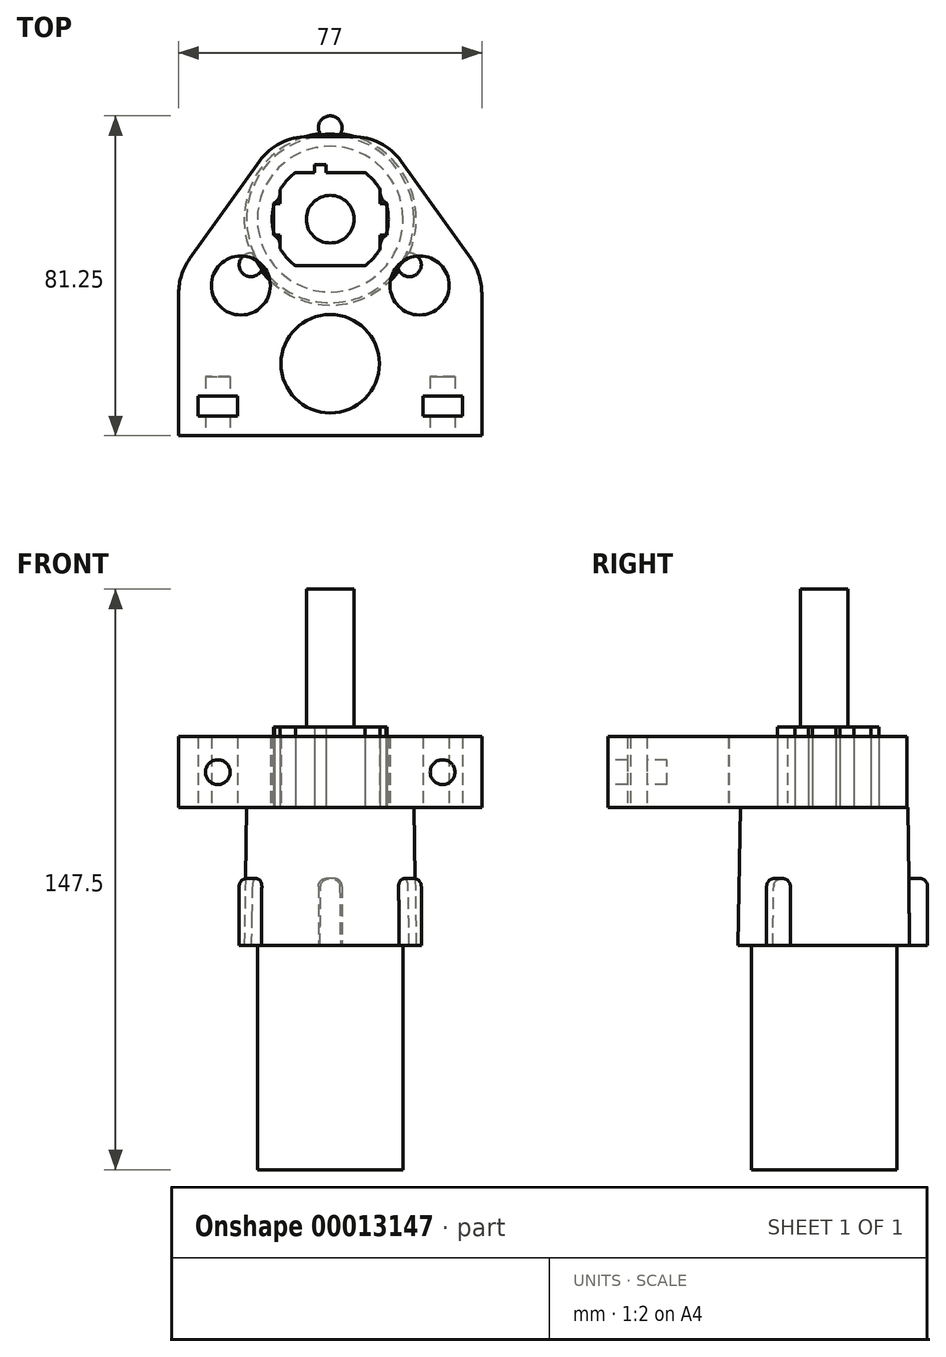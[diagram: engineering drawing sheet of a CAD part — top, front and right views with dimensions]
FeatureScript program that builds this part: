
annotation { "Feature Type Name" : "Feature", "Feature Type Description" : "" }
export const myFeature = defineFeature(function(context is Context, id is Id, definition is map)
    precondition{}
    {
        {
            var Q0;
            Q0=qCreatedBy(makeId("Top.planeOp"),FACE);
            var sketch = newSketch(context, id + "F0", { "sketchPlane" : qUnion([Q0])});
            skCircle(sketch, "E0", {"center": v(0, 0) * mm, "radius": 18.5 * mm});
            skSolve(sketch);
        }
        {
            var Q0;
            Q0=makeQuery(id+"F0.imprint","IMPRINT",FACE,{"disambiguationData":[TD([[makeQuery(id+"F0.imprint","IMPRINT",EDGE,{"derivedFrom":sQuery(id+"F0.wireOp",EDGE,"E0")}),1.0]])]});
            extrude(context, id + "F1", {"entities" : qUnion([Q0]), "depth" : 57 * mm});
        }
        {
            var Q0;
            Q0=makeQuery(id+"F1.opExtrude","CAP_FACE",FACE,{"disambiguationData":[OSD([sQuery(id+"F0.wireOp",EDGE,"E0")])],"isStart":false});
            cPlane(context, id + "F2", {"entities" : qUnion([Q0]), "cplaneType" : CPlaneType.OFFSET, "offset" : 0 * mm, "width" : 150 * mm, "height" : 150 * mm});
        }
        {
            var Q0;
            Q0=qCreatedBy(id+"F2.planeOp",FACE);
            var sketch = newSketch(context, id + "F3", { "sketchPlane" : qUnion([Q0])});
            skCircle(sketch, "E1", {"center": v(0, 0) * mm, "radius": 23.25 * mm});
            skCircle(sketch, "E2", {"center": v(0, 23.25) * mm, "radius": 3 * mm});
            skCircle(sketch, "E3.1.0", {"center": v(-20.14, -11.62) * mm, "radius": 3 * mm});
            skCircle(sketch, "E3.2.0", {"center": v(20.14, -11.63) * mm, "radius": 3 * mm});
            skCircle(sketch, "E4", {"center": v(0, 0) * mm, "radius": 20 * mm});
            skSolve(sketch);
        }
        {
            var Q0;
            Q0=makeQuery(id+"F3.imprint","IMPRINT",FACE,{"disambiguationData":[TD([[makeQuery(id+"F3.imprint","IMPRINT",EDGE,{"derivedFrom":sQuery(id+"F3.wireOp",EDGE,"E4")}),-1.0]])]});
            var Q1;
            Q1=makeQuery(id+"F3.imprint","IMPRINT",FACE,{"disambiguationData":[TD([[makeQuery(id+"F3.imprint","IMPRINT",EDGE,{"derivedFrom":sQuery(id+"F3.wireOp",EDGE,"E4")}),1.0]])]});
            extrude(context, id + "F4", {"entities" : qUnion([Q0, Q1]), "depth" : 4.1 * mm});
        }
        {
            var Q0;
            {var subQ0=sQuery(id+"F3.wireOp",EDGE,"E1");var subQ1=sQuery(id+"F3.wireOp",EDGE,"E3.2.0");var subQ3=makeQuery(id+"F3.imprint","INTERSECT",VERTEX,{"disambiguationData":[OD(0.0)],"derivedFrom":[subQ1,subQ0]});Q0=makeQuery(id+"F3.imprint","IMPRINT",FACE,{"disambiguationData":[TD([[makeQuery(id+"F3.imprint","IMPRINT",EDGE,{"disambiguationData":[TD([[subQ3,1.0]])],"derivedFrom":subQ1}),1.0]])]});}
            var Q1;
            {var subQ0=sQuery(id+"F3.wireOp",EDGE,"E1");var subQ1=sQuery(id+"F3.wireOp",EDGE,"E3.2.0");var subQ3=makeQuery(id+"F3.imprint","INTERSECT",VERTEX,{"disambiguationData":[OD(0.0)],"derivedFrom":[subQ1,subQ0]});Q1=makeQuery(id+"F3.imprint","IMPRINT",FACE,{"disambiguationData":[TD([[makeQuery(id+"F3.imprint","IMPRINT",EDGE,{"disambiguationData":[TD([[subQ3,-1.0]])],"derivedFrom":subQ1}),1.0]])]});}
            var Q2;
            {var subQ0=sQuery(id+"F3.wireOp",EDGE,"E1");var subQ1=sQuery(id+"F3.wireOp",EDGE,"E3.1.0");var subQ3=makeQuery(id+"F3.imprint","INTERSECT",VERTEX,{"disambiguationData":[OD(0.0)],"derivedFrom":[subQ1,subQ0]});Q2=makeQuery(id+"F3.imprint","IMPRINT",FACE,{"disambiguationData":[TD([[makeQuery(id+"F3.imprint","IMPRINT",EDGE,{"disambiguationData":[TD([[subQ3,1.0]])],"derivedFrom":subQ1}),1.0]])]});}
            var Q3;
            {var subQ0=sQuery(id+"F3.wireOp",EDGE,"E1");var subQ1=sQuery(id+"F3.wireOp",EDGE,"E3.1.0");var subQ3=makeQuery(id+"F3.imprint","INTERSECT",VERTEX,{"disambiguationData":[OD(0.0)],"derivedFrom":[subQ1,subQ0]});Q3=makeQuery(id+"F3.imprint","IMPRINT",FACE,{"disambiguationData":[TD([[makeQuery(id+"F3.imprint","IMPRINT",EDGE,{"disambiguationData":[TD([[subQ3,-1.0]])],"derivedFrom":subQ1}),1.0]])]});}
            var Q4;
            {var subQ0=sQuery(id+"F3.wireOp",EDGE,"E1");var subQ1=sQuery(id+"F3.wireOp",EDGE,"E2");var subQ3=makeQuery(id+"F3.imprint","INTERSECT",VERTEX,{"disambiguationData":[OD(0.0)],"derivedFrom":[subQ1,subQ0]});Q4=makeQuery(id+"F3.imprint","IMPRINT",FACE,{"disambiguationData":[TD([[makeQuery(id+"F3.imprint","IMPRINT",EDGE,{"disambiguationData":[TD([[subQ3,-1.0]])],"derivedFrom":subQ1}),1.0]])]});}
            var Q5;
            {var subQ0=sQuery(id+"F3.wireOp",EDGE,"E1");var subQ1=sQuery(id+"F3.wireOp",EDGE,"E2");var subQ3=makeQuery(id+"F3.imprint","INTERSECT",VERTEX,{"disambiguationData":[OD(0.0)],"derivedFrom":[subQ1,subQ0]});Q5=makeQuery(id+"F3.imprint","IMPRINT",FACE,{"disambiguationData":[TD([[makeQuery(id+"F3.imprint","IMPRINT",EDGE,{"disambiguationData":[TD([[subQ3,1.0]])],"derivedFrom":subQ1}),1.0]])]});}
            extrude(context, id + "F5", {"entities" : qUnion([Q0, Q1, Q2, Q3, Q4, Q5]), "operationType" : NewBodyOperationType.ADD, "depth" : 17 * mm});
        }
        {
            var Q0;
            Q0=makeQuery(id+"F5.opExtrude","CAP_FACE",FACE,{"disambiguationData":[OSD([sQuery(id+"F3.wireOp",EDGE,"E3.2.0")])],"isStart":false});
            var Q1;
            Q1=makeQuery(id+"F5.opExtrude","CAP_FACE",FACE,{"disambiguationData":[OSD([sQuery(id+"F3.wireOp",EDGE,"E3.1.0")])],"isStart":false});
            var Q2;
            Q2=makeQuery(id+"F5.opExtrude","CAP_FACE",FACE,{"disambiguationData":[OSD([sQuery(id+"F3.wireOp",EDGE,"E2")])],"isStart":false});
            fillet(context, id + "F6", {"entities" : qUnion([Q0, Q1, Q2]), "radius" : 2 * mm, "tangentPropagation" : true, "allowEdgeOverflow" : false});
        }
        {
            var Q0;
            Q0=makeQuery(id+"F3.imprint","IMPRINT",FACE,{"disambiguationData":[TD([[makeQuery(id+"F3.imprint","IMPRINT",EDGE,{"derivedFrom":sQuery(id+"F3.wireOp",EDGE,"E4")}),1.0]])]});
            var Q1;
            Q1=makeQuery(id+"F3.imprint","IMPRINT",FACE,{"disambiguationData":[TD([[makeQuery(id+"F3.imprint","IMPRINT",EDGE,{"derivedFrom":sQuery(id+"F3.wireOp",EDGE,"E4")}),-1.0]])]});
            var Q2;
            {var subQ0=sQuery(id+"F3.wireOp",EDGE,"E1");var subQ1=sQuery(id+"F3.wireOp",EDGE,"E3.2.0");var subQ3=makeQuery(id+"F3.imprint","INTERSECT",VERTEX,{"disambiguationData":[OD(0.0)],"derivedFrom":[subQ1,subQ0]});Q2=makeQuery(id+"F3.imprint","IMPRINT",FACE,{"disambiguationData":[TD([[makeQuery(id+"F3.imprint","IMPRINT",EDGE,{"disambiguationData":[TD([[subQ3,1.0]])],"derivedFrom":subQ1}),1.0]])]});}
            var Q3;
            {var subQ0=sQuery(id+"F3.wireOp",EDGE,"E1");var subQ1=sQuery(id+"F3.wireOp",EDGE,"E3.1.0");var subQ3=makeQuery(id+"F3.imprint","INTERSECT",VERTEX,{"disambiguationData":[OD(0.0)],"derivedFrom":[subQ1,subQ0]});Q3=makeQuery(id+"F3.imprint","IMPRINT",FACE,{"disambiguationData":[TD([[makeQuery(id+"F3.imprint","IMPRINT",EDGE,{"disambiguationData":[TD([[subQ3,1.0]])],"derivedFrom":subQ1}),1.0]])]});}
            var Q4;
            {var subQ0=sQuery(id+"F3.wireOp",EDGE,"E1");var subQ1=sQuery(id+"F3.wireOp",EDGE,"E2");var subQ3=makeQuery(id+"F3.imprint","INTERSECT",VERTEX,{"disambiguationData":[OD(0.0)],"derivedFrom":[subQ1,subQ0]});Q4=makeQuery(id+"F3.imprint","IMPRINT",FACE,{"disambiguationData":[TD([[makeQuery(id+"F3.imprint","IMPRINT",EDGE,{"disambiguationData":[TD([[subQ3,-1.0]])],"derivedFrom":subQ1}),1.0]])]});}
            extrude(context, id + "F7", {"entities" : qUnion([Q0, Q1, Q2, Q3, Q4]), "operationType" : NewBodyOperationType.ADD, "depth" : 35 * mm});
        }
        {
            var Q0;
            Q0=makeQuery(id+"F7.opExtrude","CAP_FACE",FACE,{"disambiguationData":[OSD([sQuery(id+"F3.wireOp",EDGE,"E1")])],"isStart":false});
            chamfer(context, id + "F8", {"entities" : qUnion([Q0]), "chamferType" : ChamferType.OFFSET_ANGLE, "width" : 2 * mm, "oppositeDirection" : false, "angle" : 89 * degree, "tangentPropagation" : true});
        }
        {
            var Q0;
            Q0=makeQuery(id+"F7.opExtrude","CAP_FACE",FACE,{"disambiguationData":[OSD([sQuery(id+"F3.wireOp",EDGE,"E1")])],"isStart":false});
            var sketch = newSketch(context, id + "F9", { "sketchPlane" : qUnion([Q0])});
            skCircle(sketch, "E5", {"center": v(0, 0) * mm, "radius": 14.75 * mm, "construction": true});
            skLineSegment(sketch, "E6", {"start": v(-30.55, 11.85) * mm, "end": v(36.28, 11.85) * mm, "construction": true});
            skLineSegment(sketch, "E7", {"start": v(35.19, -11.85) * mm, "end": v(-8.78, -11.85) * mm, "construction": true});
            skLineSegment(sketch, "E8", {"start": v(-12.7, 34.38) * mm, "end": v(-12.7, -35.47) * mm, "construction": true});
            skLineSegment(sketch, "E9", {"start": v(12.7, 35.2) * mm, "end": v(12.7, -37.39) * mm, "construction": true});
            skLineSegment(sketch, "E10.bottom", {"start": v(-14.45, 4) * mm, "end": v(14.45, 4) * mm, "construction": true});
            skLineSegment(sketch, "E10.top", {"start": v(-14.45, -4) * mm, "end": v(14.45, -4) * mm, "construction": true});
            skLineSegment(sketch, "E10.left", {"start": v(-14.45, 4) * mm, "end": v(-14.45, -4) * mm, "construction": true});
            skLineSegment(sketch, "E10.right", {"start": v(14.45, 4) * mm, "end": v(14.45, -4) * mm});
            skLineSegment(sketch, "E11", {"start": v(-14.45, -4) * mm, "end": v(-14.45, 4) * mm});
            skLineSegment(sketch, "E12", {"start": v(-12.7, 4) * mm, "end": v(-12.7, 7.5) * mm});
            skLineSegment(sketch, "E13", {"start": v(-12.7, -7.5) * mm, "end": v(-12.7, -4) * mm});
            skLineSegment(sketch, "E14", {"start": v(-12.7, -4) * mm, "end": v(-14.45, -4) * mm});
            skLineSegment(sketch, "E15", {"start": v(-14.45, 4) * mm, "end": v(-12.7, 4) * mm});
            skLineSegment(sketch, "E16", {"start": v(12.7, -7.5) * mm, "end": v(12.7, -4) * mm});
            skLineSegment(sketch, "E17", {"start": v(12.7, -4) * mm, "end": v(14.45, -4) * mm});
            skLineSegment(sketch, "E18", {"start": v(14.45, 4) * mm, "end": v(12.7, 4) * mm});
            skLineSegment(sketch, "E19", {"start": v(12.7, 4) * mm, "end": v(12.7, 7.5) * mm});
            skLineSegment(sketch, "E20", {"start": v(-8.78, -11.85) * mm, "end": v(-31.65, -11.85) * mm, "construction": true});
            skLineSegment(sketch, "E21", {"start": v(-8.78, 11.85) * mm, "end": v(-4, 11.85) * mm});
            skLineSegment(sketch, "E22", {"start": v(-8.78, -11.85) * mm, "end": v(8.78, -11.85) * mm});
            skLineSegment(sketch, "E23.top", {"start": v(-1, 13.85) * mm, "end": v(-4, 13.85) * mm});
            skLineSegment(sketch, "E23.left", {"start": v(-1, 11.85) * mm, "end": v(-1, 13.85) * mm});
            skLineSegment(sketch, "E23.right", {"start": v(-4, 11.85) * mm, "end": v(-4, 13.85) * mm});
            skPoint(sketch, "E24", {"position": v(0, 11.85) * mm});
            skLineSegment(sketch, "E25", {"start": v(-1, 11.85) * mm, "end": v(8.78, 11.85) * mm});
            skLineSegment(sketch, "E26.bottom", {"start": v(-38.5, -55) * mm, "end": v(0, -55) * mm});
            skLineSegment(sketch, "E26.top", {"start": v(-38.5, 21) * mm, "end": v(38.5, 21) * mm});
            skLineSegment(sketch, "E26.left", {"start": v(-38.5, -55) * mm, "end": v(-38.5, 21) * mm});
            skLineSegment(sketch, "E26.right", {"start": v(38.5, -55) * mm, "end": v(38.5, 21) * mm});
            skPoint(sketch, "E27", {"position": v(0, -55) * mm});
            skLineSegment(sketch, "E28", {"start": v(0, -55) * mm, "end": v(38.5, -55) * mm});
            skLineSegment(sketch, "E29.bottom", {"start": v(-33.55, -45) * mm, "end": v(-23.55, -45) * mm});
            skLineSegment(sketch, "E29.top", {"start": v(-33.55, -50) * mm, "end": v(-28.55, -50) * mm});
            skLineSegment(sketch, "E29.left", {"start": v(-33.55, -45) * mm, "end": v(-33.55, -50) * mm});
            skLineSegment(sketch, "E29.right", {"start": v(-23.55, -45) * mm, "end": v(-23.55, -50) * mm});
            skPoint(sketch, "E30", {"position": v(-28.55, -50) * mm});
            skLineSegment(sketch, "E31", {"start": v(-28.55, -50) * mm, "end": v(-23.55, -50) * mm});
            skLineSegment(sketch, "E32", {"start": v(-28.55, -20.18) * mm, "end": v(-28.55, -60.95) * mm, "construction": true});
            skLineSegment(sketch, "E33", {"start": v(28.55, -21.34) * mm, "end": v(28.55, -62.11) * mm, "construction": true});
            skLineSegment(sketch, "E34", {"start": v(0, -55) * mm, "end": v(28.55, -55) * mm, "construction": true});
            skLineSegment(sketch, "E35", {"start": v(-28.55, -55) * mm, "end": v(0, -55) * mm, "construction": true});
            skLineSegment(sketch, "E36", {"start": v(-28.55, -55) * mm, "end": v(0, -55) * mm});
            skLineSegment(sketch, "E37", {"start": v(0, -55) * mm, "end": v(28.55, -55) * mm});
            skPoint(sketch, "E38.1.0.0", {"position": v(28.55, -50) * mm});
            skLineSegment(sketch, "E38.1.0.1", {"start": v(23.55, -45) * mm, "end": v(23.55, -50) * mm});
            skLineSegment(sketch, "E38.1.0.2", {"start": v(23.55, -45) * mm, "end": v(33.55, -45) * mm});
            skLineSegment(sketch, "E38.1.0.3", {"start": v(23.55, -50) * mm, "end": v(28.55, -50) * mm});
            skLineSegment(sketch, "E38.1.0.4", {"start": v(33.55, -45) * mm, "end": v(33.55, -50) * mm});
            skLineSegment(sketch, "E38.1.0.5", {"start": v(28.55, -50) * mm, "end": v(33.55, -50) * mm});
            skLineSegment(sketch, "E38.direction1", {"start": v(-28.55, -50) * mm, "end": v(0, -50) * mm, "construction": true});
            skCircle(sketch, "E39", {"center": v(0, -36.74) * mm, "radius": 12.5 * mm});
            skLineSegment(sketch, "E40", {"start": v(-46.69, -16.85) * mm, "end": v(42.09, -16.85) * mm, "construction": true});
            skCircle(sketch, "E41", {"center": v(-22.7, -16.85) * mm, "radius": 7.5 * mm});
            skCircle(sketch, "E42", {"center": v(22.7, -16.85) * mm, "radius": 7.5 * mm});
            skPoint(sketch, "E43", {"position": v(0, -50) * mm});
            skLineSegment(sketch, "E44", {"start": v(0, -50) * mm, "end": v(28.55, -50) * mm, "construction": true});
            skPoint(sketch, "E45", {"position": v(-14.45, 0) * mm});
            skCircle(sketch, "E46", {"center": v(0, 0) * mm, "radius": 14.75 * mm});
            skPoint(sketch, "E47", {"position": v(-28.55, -55) * mm});
            skPoint(sketch, "E48", {"position": v(28.55, -55) * mm});
            skSolve(sketch);
        }
        {
            var Q0;
            {var subQ14=sQuery(id+"F9.wireOp",EDGE,"E12");Q0=makeQuery(id+"F9.imprint","IMPRINT",FACE,{"disambiguationData":[TD([[makeQuery(id+"F9.imprint","IMPRINT",EDGE,{"derivedFrom":subQ14}),-1.0]])]});}
            var Q1;
            Q1=sQuery(id+"F9.wireOp",EDGE,"f083ccfe-dad7-4127-a4e6-e0b0007866951");
            var Q2;
            Q2=sQuery(id+"F9.wireOp",EDGE,"E16");
            var Q3;
            Q3=sQuery(id+"F9.wireOp",EDGE,"E17");
            var Q4;
            Q4=sQuery(id+"F9.wireOp",EDGE,"E10.right");
            var Q5;
            Q5=sQuery(id+"F9.wireOp",EDGE,"E18");
            var Q6;
            Q6=sQuery(id+"F9.wireOp",EDGE,"E19");
            var Q7;
            Q7=sQuery(id+"F9.wireOp",EDGE,"232c7e1f-37ef-4763-9ab7-0026ba6834dc2");
            var Q8;
            Q8=sQuery(id+"F9.wireOp",EDGE,"E15");
            var Q9;
            Q9=sQuery(id+"F9.wireOp",EDGE,"E11");
            var Q10;
            Q10=sQuery(id+"F9.wireOp",EDGE,"E14");
            var Q11;
            Q11=sQuery(id+"F9.wireOp",EDGE,"E13");
            var Q12;
            Q12=sQuery(id+"F9.wireOp",EDGE,"E12");
            extrude(context, id + "F10", {"entities" : qUnion([Q0]), "surfaceEntities" : qUnion([Q1, Q2, Q3, Q4, Q5, Q6, Q7, Q8, Q9, Q10, Q11, Q12]), "depth" : 20.5 * mm});
        }
        {
            var Q0;
            Q0=makeQuery(id+"F10.opExtrude","CAP_FACE",FACE,{"disambiguationData":[OSD([sQuery(id+"F9.wireOp",EDGE,"E10.right"),sQuery(id+"F9.wireOp",EDGE,"E11"),sQuery(id+"F9.wireOp",EDGE,"E12"),sQuery(id+"F9.wireOp",EDGE,"E13"),sQuery(id+"F9.wireOp",EDGE,"E14"),sQuery(id+"F9.wireOp",EDGE,"E15"),sQuery(id+"F9.wireOp",EDGE,"E16"),sQuery(id+"F9.wireOp",EDGE,"E17"),sQuery(id+"F9.wireOp",EDGE,"E18"),sQuery(id+"F9.wireOp",EDGE,"E19"),sQuery(id+"F9.wireOp",EDGE,"232c7e1f-37ef-4763-9ab7-0026ba6834dc2"),sQuery(id+"F9.wireOp",EDGE,"f083ccfe-dad7-4127-a4e6-e0b0007866951")])],"isStart":false});
            var sketch = newSketch(context, id + "F11", { "sketchPlane" : qUnion([Q0])});
            skCircle(sketch, "E49", {"center": v(0, 0) * mm, "radius": 6.05 * mm});
            skSolve(sketch);
        }
        {
            var Q0;
            Q0=makeQuery(id+"F11.imprint","IMPRINT",FACE,{"disambiguationData":[TD([[makeQuery(id+"F11.imprint","IMPRINT",EDGE,{"derivedFrom":sQuery(id+"F11.wireOp",EDGE,"E49")}),1.0]])]});
            extrude(context, id + "F12", {"entities" : qUnion([Q0]), "operationType" : NewBodyOperationType.ADD, "depth" : 35 * mm});
        }
        {
            var Q0;
            Q0=makeQuery(id+"F9.imprint","IMPRINT",FACE,{"disambiguationData":[TD([[makeQuery(id+"F9.imprint","IMPRINT",EDGE,{"derivedFrom":sQuery(id+"F9.wireOp",EDGE,"E26.bottom")}),1.0]])]});
            var Q1;
            {var subQ11=sQuery(id+"F9.wireOp",EDGE,"E10.right");var subQ14=sQuery(id+"F9.wireOp",EDGE,"E18");var subQ15=makeQuery(id+"F9.imprint","INTERSECT",VERTEX,{"derivedFrom":[subQ11,subQ14]});Q1=makeQuery(id+"F9.imprint","IMPRINT",FACE,{"disambiguationData":[TD([[makeQuery(id+"F9.imprint","IMPRINT",EDGE,{"disambiguationData":[TD([[subQ15,-1.0]])],"derivedFrom":subQ11}),1.0]])]});}
            var Q2;
            {var subQ2=sQuery(id+"F9.wireOp",EDGE,"E21");Q2=makeQuery(id+"F9.imprint","IMPRINT",FACE,{"disambiguationData":[TD([[makeQuery(id+"F9.imprint","IMPRINT",EDGE,{"derivedFrom":subQ2}),1.0]])]});}
            var Q3;
            {var subQ3=sQuery(id+"F9.wireOp",EDGE,"E19");Q3=makeQuery(id+"F9.imprint","IMPRINT",FACE,{"disambiguationData":[TD([[makeQuery(id+"F9.imprint","IMPRINT",EDGE,{"derivedFrom":subQ3}),-1.0]])]});}
            var Q4;
            {var subQ3=sQuery(id+"F9.wireOp",EDGE,"E16");Q4=makeQuery(id+"F9.imprint","IMPRINT",FACE,{"disambiguationData":[TD([[makeQuery(id+"F9.imprint","IMPRINT",EDGE,{"derivedFrom":subQ3}),-1.0]])]});}
            var Q5;
            {var subQ3=sQuery(id+"F9.wireOp",EDGE,"E13");Q5=makeQuery(id+"F9.imprint","IMPRINT",FACE,{"disambiguationData":[TD([[makeQuery(id+"F9.imprint","IMPRINT",EDGE,{"derivedFrom":subQ3}),1.0]])]});}
            var Q6;
            {var subQ3=sQuery(id+"F9.wireOp",EDGE,"E12");Q6=makeQuery(id+"F9.imprint","IMPRINT",FACE,{"disambiguationData":[TD([[makeQuery(id+"F9.imprint","IMPRINT",EDGE,{"derivedFrom":subQ3}),1.0]])]});}
            var Q7;
            {var subQ1=sQuery(id+"F9.wireOp",EDGE,"E22");Q7=makeQuery(id+"F9.imprint","IMPRINT",FACE,{"disambiguationData":[TD([[makeQuery(id+"F9.imprint","IMPRINT",EDGE,{"derivedFrom":subQ1}),-1.0]])]});}
            extrude(context, id + "F13", {"entities" : qUnion([Q0, Q1, Q2, Q3, Q4, Q5, Q6, Q7]), "depth" : 18 * mm});
        }
        {
            var Q0;
            Q0=makeQuery(id+"F13.opExtrude","SWEPT_FACE",FACE,{"disambiguationData":[OSD([sQuery(id+"F9.wireOp",EDGE,"E26.bottom"),sQuery(id+"F9.wireOp",EDGE,"E28"),sQuery(id+"F9.wireOp",EDGE,"E36"),sQuery(id+"F9.wireOp",EDGE,"E37")])]});
            var sketch = newSketch(context, id + "F14", { "sketchPlane" : qUnion([Q0])});
            skLineSegment(sketch, "E50", {"start": v(-38.5, 101) * mm, "end": v(38.5, 101) * mm, "construction": true});
            skLineSegment(sketch, "E51", {"start": v(28.55, 92) * mm, "end": v(28.55, 108.48) * mm, "construction": true});
            skLineSegment(sketch, "E52", {"start": v(-28.55, 92) * mm, "end": v(-28.55, 101) * mm, "construction": true});
            skCircle(sketch, "E53", {"center": v(-28.55, 101) * mm, "radius": 3.15 * mm});
            skCircle(sketch, "E54", {"center": v(28.55, 101) * mm, "radius": 3.15 * mm});
            skPoint(sketch, "E55.0", {"position": v(28.55, 92) * mm});
            skPoint(sketch, "E56.0", {"position": v(-28.55, 92) * mm});
            skSolve(sketch);
        }
        {
            var Q0;
            Q0=makeQuery(id+"F14.imprint","IMPRINT",FACE,{"disambiguationData":[TD([[makeQuery(id+"F14.imprint","IMPRINT",EDGE,{"derivedFrom":sQuery(id+"F14.wireOp",EDGE,"E53")}),1.0]])]});
            var Q1;
            Q1=makeQuery(id+"F14.imprint","IMPRINT",FACE,{"disambiguationData":[TD([[makeQuery(id+"F14.imprint","IMPRINT",EDGE,{"derivedFrom":sQuery(id+"F14.wireOp",EDGE,"E54")}),1.0]])]});
            extrude(context, id + "F15", {"entities" : qUnion([Q0, Q1]), "operationType" : NewBodyOperationType.REMOVE, "oppositeDirection" : true, "depth" : 15 * mm});
        }
        {
            var Q0;
            Q0=makeQuery(id+"F13.opExtrude","SWEPT_EDGE",EDGE,{"disambiguationData":[OSD([sQuery(id+"F9.wireOp",EDGE,"E26.top"),sQuery(id+"F9.wireOp",EDGE,"E26.right")])]});
            var Q1;
            Q1=makeQuery(id+"F13.opExtrude","SWEPT_EDGE",EDGE,{"disambiguationData":[OSD([sQuery(id+"F9.wireOp",EDGE,"E26.top"),sQuery(id+"F9.wireOp",EDGE,"E26.left")])]});
            chamfer(context, id + "F16", {"entities" : qUnion([Q0, Q1]), "chamferType" : ChamferType.TWO_OFFSETS, "width1" : 25 * mm, "oppositeDirection" : false, "width2" : 35 * mm, "tangentPropagation" : true});
        }
        {
            var Q0;
            {var subQ0=sQuery(id+"F9.wireOp",EDGE,"E26.right");Q0=makeQuery(id+"F16.opChamfer","BLEND_EDGE",EDGE,{"blendedFrom":[makeQuery(id+"F13.opExtrude","SWEPT_EDGE",EDGE,{"disambiguationData":[OSD([sQuery(id+"F9.wireOp",EDGE,"E26.top"),subQ0])]}),makeQuery(id+"F13.opExtrude","SWEPT_FACE",FACE,{"disambiguationData":[OSD([subQ0])]})],"blendedInto":[makeQuery(id+"F13.opExtrude","SWEPT_FACE",FACE,{"disambiguationData":[OSD([subQ0])]})]});}
            var Q1;
            {var subQ0=sQuery(id+"F9.wireOp",EDGE,"E26.top");Q1=makeQuery(id+"F16.opChamfer","BLEND_EDGE",EDGE,{"blendedFrom":[makeQuery(id+"F13.opExtrude","SWEPT_EDGE",EDGE,{"disambiguationData":[OSD([subQ0,sQuery(id+"F9.wireOp",EDGE,"E26.right")])]}),makeQuery(id+"F13.opExtrude","SWEPT_FACE",FACE,{"disambiguationData":[OSD([subQ0])]})],"blendedInto":[makeQuery(id+"F13.opExtrude","SWEPT_FACE",FACE,{"disambiguationData":[OSD([subQ0])]})]});}
            var Q2;
            {var subQ0=sQuery(id+"F9.wireOp",EDGE,"E26.top");Q2=makeQuery(id+"F16.opChamfer","BLEND_EDGE",EDGE,{"blendedFrom":[makeQuery(id+"F13.opExtrude","SWEPT_EDGE",EDGE,{"disambiguationData":[OSD([subQ0,sQuery(id+"F9.wireOp",EDGE,"E26.left")])]}),makeQuery(id+"F13.opExtrude","SWEPT_FACE",FACE,{"disambiguationData":[OSD([subQ0])]})],"blendedInto":[makeQuery(id+"F13.opExtrude","SWEPT_FACE",FACE,{"disambiguationData":[OSD([subQ0])]})]});}
            var Q3;
            {var subQ0=sQuery(id+"F9.wireOp",EDGE,"E26.left");Q3=makeQuery(id+"F16.opChamfer","BLEND_EDGE",EDGE,{"blendedFrom":[makeQuery(id+"F13.opExtrude","SWEPT_EDGE",EDGE,{"disambiguationData":[OSD([sQuery(id+"F9.wireOp",EDGE,"E26.top"),subQ0])]}),makeQuery(id+"F13.opExtrude","SWEPT_FACE",FACE,{"disambiguationData":[OSD([subQ0])]})],"blendedInto":[makeQuery(id+"F13.opExtrude","SWEPT_FACE",FACE,{"disambiguationData":[OSD([subQ0])]})]});}
            fillet(context, id + "F17", {"entities" : qUnion([Q0, Q1, Q2, Q3]), "radius" : 15 * mm, "tangentPropagation" : true, "allowEdgeOverflow" : false});
        }
        {
            var Q0;
            Q0=makeQuery(id+"F13.opExtrude","SWEPT_EDGE",EDGE,{"disambiguationData":[OSD([sQuery(id+"F9.wireOp",EDGE,"E18"),sQuery(id+"F9.wireOp",EDGE,"E19")])]});
            var Q1;
            Q1=makeQuery(id+"F13.opExtrude","SWEPT_EDGE",EDGE,{"disambiguationData":[OSD([sQuery(id+"F9.wireOp",EDGE,"E16"),sQuery(id+"F9.wireOp",EDGE,"E17")])]});
            var Q2;
            Q2=makeQuery(id+"F13.opExtrude","SWEPT_EDGE",EDGE,{"disambiguationData":[OSD([sQuery(id+"F9.wireOp",EDGE,"E13"),sQuery(id+"F9.wireOp",EDGE,"E14")])]});
            var Q3;
            Q3=makeQuery(id+"F13.opExtrude","SWEPT_EDGE",EDGE,{"disambiguationData":[OSD([sQuery(id+"F9.wireOp",EDGE,"E12"),sQuery(id+"F9.wireOp",EDGE,"E15")])]});
            fillet(context, id + "F18", {"entities" : qUnion([Q0, Q1, Q2, Q3]), "radius" : 3 * mm, "tangentPropagation" : true, "allowEdgeOverflow" : false});
        }
    });
